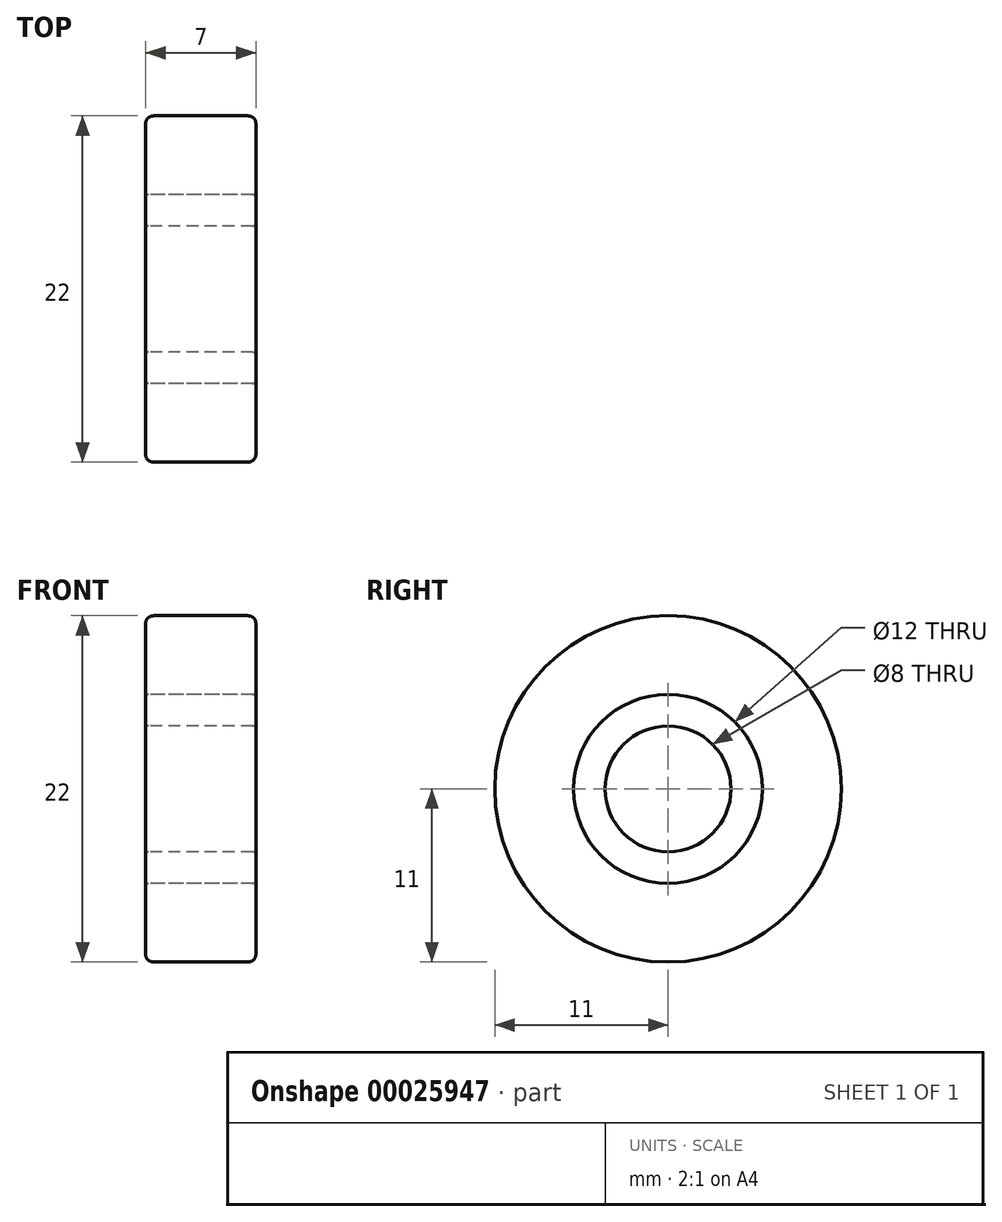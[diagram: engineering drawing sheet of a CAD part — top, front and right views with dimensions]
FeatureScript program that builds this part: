
annotation { "Feature Type Name" : "Feature", "Feature Type Description" : "" }
export const myFeature = defineFeature(function(context is Context, id is Id, definition is map)
    precondition{}
    {
        {
            var Q0;
            Q0=qCreatedBy(makeId("Right.planeOp"),FACE);
            var sketch = newSketch(context, id + "F0", { "sketchPlane" : qUnion([Q0])});
            skCircle(sketch, "E0", {"center": v(0, 0) * mm, "radius": 4 * mm});
            skCircle(sketch, "E1", {"center": v(0, 0) * mm, "radius": 11 * mm});
            skCircle(sketch, "E2", {"center": v(0, 0) * mm, "radius": 6 * mm});
            skSolve(sketch);
        }
        {
            var Q0;
            Q0=makeQuery(id+"F0.imprint","IMPRINT",FACE,{"disambiguationData":[TD([[makeQuery(id+"F0.imprint","IMPRINT",EDGE,{"derivedFrom":sQuery(id+"F0.wireOp",EDGE,"E0")}),-1.0]])]});
            extrude(context, id + "F1", {"entities" : qUnion([Q0]), "depth" : 7 * mm});
        }
        {
            var Q0;
            Q0=makeQuery(id+"F0.imprint","IMPRINT",FACE,{"disambiguationData":[TD([[makeQuery(id+"F0.imprint","IMPRINT",EDGE,{"derivedFrom":sQuery(id+"F0.wireOp",EDGE,"E1")}),1.0]])]});
            extrude(context, id + "F2", {"entities" : qUnion([Q0]), "depth" : 7 * mm});
        }
        {
            var Q0;
            Q0=makeQuery(id+"F2.opExtrude","CAP_EDGE",EDGE,{"disambiguationData":[OSD([sQuery(id+"F0.wireOp",EDGE,"E1")])],"isStart":false});
            var Q1;
            Q1=makeQuery(id+"F2.opExtrude","CAP_EDGE",EDGE,{"disambiguationData":[OSD([sQuery(id+"F0.wireOp",EDGE,"E1")])],"isStart":true});
            fillet(context, id + "F3", {"entities" : qUnion([Q0, Q1]), "radius" : .5 * mm, "tangentPropagation" : true, "allowEdgeOverflow" : false});
        }
        {
            var Q0;
            Q0=makeQuery(id+"F1.opExtrude","CAP_EDGE",EDGE,{"disambiguationData":[OSD([sQuery(id+"F0.wireOp",EDGE,"E0")])],"isStart":false});
            var Q1;
            Q1=makeQuery(id+"F1.opExtrude","CAP_EDGE",EDGE,{"disambiguationData":[OSD([sQuery(id+"F0.wireOp",EDGE,"E2")])],"isStart":false});
            var Q2;
            Q2=makeQuery(id+"F1.opExtrude","CAP_EDGE",EDGE,{"disambiguationData":[OSD([sQuery(id+"F0.wireOp",EDGE,"E2")])],"isStart":true});
            var Q3;
            Q3=makeQuery(id+"F1.opExtrude","CAP_EDGE",EDGE,{"disambiguationData":[OSD([sQuery(id+"F0.wireOp",EDGE,"E0")])],"isStart":true});
            fillet(context, id + "F4", {"entities" : qUnion([Q0, Q1, Q2, Q3]), "radius" : .2 * mm, "tangentPropagation" : true, "allowEdgeOverflow" : false});
        }
    });
